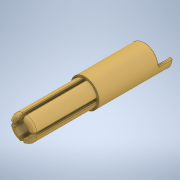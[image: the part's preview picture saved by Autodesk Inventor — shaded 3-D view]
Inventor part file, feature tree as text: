
AUTODESK INVENTOR PART (.ipt)
format: ipt  version: 2020.1 (Build 241239000, 239)  size: 275,456 bytes
history: native  units: mm
features: sketch x1
ambient origin geometry x8: Origin, YZ Plane, XZ Plane, XY Plane, X Axis, Y Axis, Z Axis, Center Point
bodies: Solid2 (feature_tree), Solid1 (feature_tree)
feature tree (1):
  sketch  "Sketch1"
